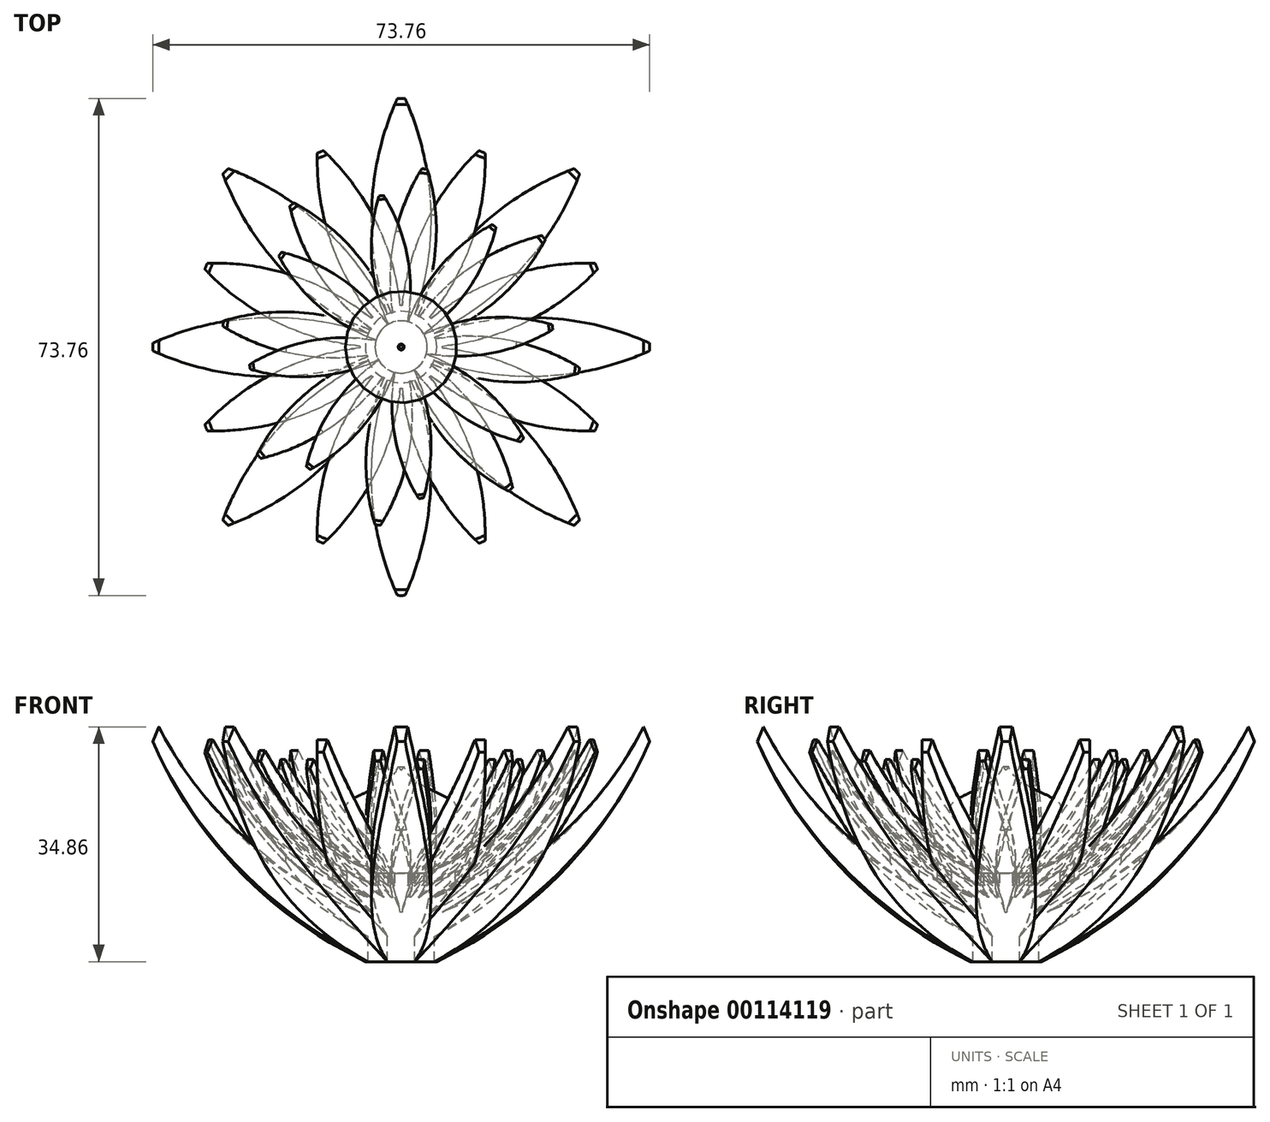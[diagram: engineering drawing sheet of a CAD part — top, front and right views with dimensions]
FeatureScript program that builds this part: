
annotation { "Feature Type Name" : "Feature", "Feature Type Description" : "" }
export const myFeature = defineFeature(function(context is Context, id is Id, definition is map)
    precondition{}
    {
        {
            var Q0;
            Q0=qCreatedBy(makeId("Top.planeOp"),FACE);
            var sketch = newSketch(context, id + "F0", { "sketchPlane" : qUnion([Q0])});
            skLineSegment(sketch, "E0.bottom", {"start": v(38.1, -38.1) * mm, "end": v(-38.1, -38.1) * mm});
            skLineSegment(sketch, "E0.top", {"start": v(38.1, 38.1) * mm, "end": v(-38.1, 38.1) * mm});
            skLineSegment(sketch, "E0.left", {"start": v(38.1, -38.1) * mm, "end": v(38.1, 38.1) * mm});
            skLineSegment(sketch, "E0.right", {"start": v(-38.1, -38.1) * mm, "end": v(-38.1, 38.1) * mm});
            skPoint(sketch, "E0.middle", {"position": v(0, 0) * mm});
            skSolve(sketch);
        }
        {
            var Q0;
            Q0 = qSketchRegion(id + "F0", true);
            extrude(context, id + "F1", {"entities" : qUnion([Q0]), "depth" : 50.8 * mm});
        }
        {
            var Q0;
            Q0=makeQuery(id+"F1.opExtrude","CAP_FACE",FACE,{"disambiguationData":[OSD([sQuery(id+"F0.wireOp",EDGE,"E0.bottom"),sQuery(id+"F0.wireOp",EDGE,"E0.top"),sQuery(id+"F0.wireOp",EDGE,"E0.left"),sQuery(id+"F0.wireOp",EDGE,"E0.right")])],"isStart":false});
            var sketch = newSketch(context, id + "F2", { "sketchPlane" : qUnion([Q0])});
            skCircle(sketch, "E1", {"center": v(0, 0) * mm, "radius": 3.18 * mm, "construction": true});
            skLineSegment(sketch, "E2", {"start": v(-38.1, 38.1) * mm, "end": v(38.1, -38.1) * mm, "construction": true});
            skLineSegment(sketch, "E3", {"start": v(38.1, 38.1) * mm, "end": v(-38.1, -38.1) * mm, "construction": true});
            skLineSegment(sketch, "E4", {"start": v(0, -38.1) * mm, "end": v(0, 38.1) * mm, "construction": true});
            skLineSegment(sketch, "E5", {"start": v(-38.1, 0) * mm, "end": v(38.1, 0) * mm, "construction": true});
            skLineSegment(sketch, "E6.bottom", {"start": v(-38.1, 38.1) * mm, "end": v(38.1, 38.1) * mm});
            skLineSegment(sketch, "E6.top", {"start": v(-38.1, -38.1) * mm, "end": v(38.1, -38.1) * mm});
            skLineSegment(sketch, "E6.left", {"start": v(-38.1, 38.1) * mm, "end": v(-38.1, -38.1) * mm});
            skLineSegment(sketch, "E6.right", {"start": v(38.1, 38.1) * mm, "end": v(38.1, -38.1) * mm});
            skArc(sketch, "E7", {"start": v(0, 0) * mm, "mid": v(4.4, 19.05) * mm, "end": v(0, 38.1) * mm});
            skArc(sketch, "E8.MirrorCS", {"start": v(0, 0) * mm, "mid": v(-4.4, 19.05) * mm, "end": v(0, 38.1) * mm});
            skArc(sketch, "E9.1.0", {"start": v(0, 0) * mm, "mid": v(-10.36, 16.58) * mm, "end": v(-26.94, 26.94) * mm});
            skArc(sketch, "E9.1.1", {"start": v(0, 0) * mm, "mid": v(-16.58, 10.36) * mm, "end": v(-26.94, 26.94) * mm});
            skArc(sketch, "E9.2.0", {"start": v(0, 0) * mm, "mid": v(-19.05, 4.4) * mm, "end": v(-38.1, 0) * mm});
            skArc(sketch, "E9.2.1", {"start": v(0, 0) * mm, "mid": v(-19.05, -4.4) * mm, "end": v(-38.1, 0) * mm});
            skArc(sketch, "E9.3.0", {"start": v(0, 0) * mm, "mid": v(-16.58, -10.36) * mm, "end": v(-26.94, -26.94) * mm});
            skArc(sketch, "E9.3.1", {"start": v(0, 0) * mm, "mid": v(-10.36, -16.58) * mm, "end": v(-26.94, -26.94) * mm});
            skArc(sketch, "E9.4.0", {"start": v(0, 0) * mm, "mid": v(-4.4, -19.05) * mm, "end": v(0, -38.1) * mm});
            skArc(sketch, "E9.4.1", {"start": v(0, 0) * mm, "mid": v(4.4, -19.05) * mm, "end": v(0, -38.1) * mm});
            skArc(sketch, "E9.5.0", {"start": v(0, 0) * mm, "mid": v(10.36, -16.58) * mm, "end": v(26.94, -26.94) * mm});
            skArc(sketch, "E9.5.1", {"start": v(0, 0) * mm, "mid": v(16.58, -10.36) * mm, "end": v(26.94, -26.94) * mm});
            skArc(sketch, "E9.6.0", {"start": v(0, 0) * mm, "mid": v(19.05, -4.4) * mm, "end": v(38.1, 0) * mm});
            skArc(sketch, "E9.6.1", {"start": v(0, 0) * mm, "mid": v(19.05, 4.4) * mm, "end": v(38.1, 0) * mm});
            skArc(sketch, "E9.7.0", {"start": v(0, 0) * mm, "mid": v(16.58, 10.36) * mm, "end": v(26.94, 26.94) * mm});
            skArc(sketch, "E9.7.1", {"start": v(0, 0) * mm, "mid": v(10.36, 16.58) * mm, "end": v(26.94, 26.94) * mm});
            skSolve(sketch);
        }
        {
            var Q0;
            {var subQ0=sQuery(id+"F2.wireOp",EDGE,"E9.1.1");var subQ1=sQuery(id+"F2.wireOp",EDGE,"E9.1.0");var subQ2=makeQuery(id+"F2.imprint","INTERSECT",VERTEX,{"derivedFrom":[subQ1,subQ0]});Q0=makeQuery(id+"F2.imprint","IMPRINT",FACE,{"disambiguationData":[TD([[makeQuery(id+"F2.imprint","IMPRINT",EDGE,{"disambiguationData":[TD([[subQ2,1.0]])],"derivedFrom":subQ1}),-1.0]])]});}
            var Q1;
            {var subQ0=sQuery(id+"F2.wireOp",EDGE,"E9.5.1");var subQ1=sQuery(id+"F2.wireOp",EDGE,"E9.5.0");var subQ2=makeQuery(id+"F2.imprint","INTERSECT",VERTEX,{"derivedFrom":[subQ1,subQ0]});Q1=makeQuery(id+"F2.imprint","IMPRINT",FACE,{"disambiguationData":[TD([[makeQuery(id+"F2.imprint","IMPRINT",EDGE,{"disambiguationData":[TD([[subQ2,1.0]])],"derivedFrom":subQ1}),-1.0]])]});}
            var Q2;
            {var subQ0=sQuery(id+"F2.wireOp",EDGE,"E9.3.1");var subQ1=sQuery(id+"F2.wireOp",EDGE,"E9.3.0");var subQ2=makeQuery(id+"F2.imprint","INTERSECT",VERTEX,{"derivedFrom":[subQ1,subQ0]});Q2=makeQuery(id+"F2.imprint","IMPRINT",FACE,{"disambiguationData":[TD([[makeQuery(id+"F2.imprint","IMPRINT",EDGE,{"disambiguationData":[TD([[subQ2,1.0]])],"derivedFrom":subQ1}),-1.0]])]});}
            var Q3;
            {var subQ3=sQuery(id+"F2.wireOp",EDGE,"E9.7.0");var subQ9=sQuery(id+"F2.wireOp",EDGE,"E9.7.1");var subQ11=makeQuery(id+"F2.imprint","INTERSECT",VERTEX,{"derivedFrom":[subQ3,subQ9]});Q3=makeQuery(id+"F2.imprint","IMPRINT",FACE,{"disambiguationData":[TD([[makeQuery(id+"F2.imprint","IMPRINT",EDGE,{"disambiguationData":[TD([[subQ11,1.0]])],"derivedFrom":subQ3}),-1.0]])]});}
            extrude(context, id + "F3", {"entities" : qUnion([Q0, Q1, Q2, Q3]), "operationType" : NewBodyOperationType.REMOVE, "endBound" : BoundingType.THROUGH_ALL, "oppositeDirection" : true, "depth" : 25.4 * mm});
        }
        {
            var Q0;
            Q0=qCreatedBy(makeId("Front.planeOp"),FACE);
            var sketch = newSketch(context, id + "F4", { "sketchPlane" : qUnion([Q0])});
            skLineSegment(sketch, "E10", {"start": v(0, 0) * mm, "end": v(0, 58.2) * mm, "construction": true});
            skPoint(sketch, "E11.0", {"position": v(-38.1, 50.8) * mm});
            skPoint(sketch, "E11.1", {"position": v(38.1, 50.8) * mm});
            skPoint(sketch, "E11.2", {"position": v(38.1, 0) * mm});
            skPoint(sketch, "E11.3", {"position": v(-38.1, 0) * mm});
            skLineSegment(sketch, "E12.bottom", {"start": v(-38.1, 50.8) * mm, "end": v(38.1, 50.8) * mm, "construction": true});
            skLineSegment(sketch, "E12.top", {"start": v(-38.1, 0) * mm, "end": v(38.1, 0) * mm, "construction": true});
            skLineSegment(sketch, "E12.left", {"start": v(-38.1, 50.8) * mm, "end": v(-38.1, 0) * mm, "construction": true});
            skLineSegment(sketch, "E12.right", {"start": v(38.1, 50.8) * mm, "end": v(38.1, 0) * mm, "construction": true});
            skArc(sketch, "E13", {"start": v(-36, 37.1) * mm, "mid": v(-21.13, 18.5) * mm, "end": v(0, 7.51) * mm});
            skArc(sketch, "E14", {"start": v(-36.88, 34.9) * mm, "mid": v(-21.98, 13.7) * mm, "end": v(0, 0) * mm});
            skLineSegment(sketch, "E15.bottom", {"start": v(0, 64) * mm, "end": v(-47.12, 64) * mm});
            skLineSegment(sketch, "E15.top", {"start": v(0, -8.54) * mm, "end": v(-47.12, -8.54) * mm});
            skLineSegment(sketch, "E15.left", {"start": v(0, 64) * mm, "end": v(0, -8.54) * mm});
            skLineSegment(sketch, "E15.right", {"start": v(-47.12, 64) * mm, "end": v(-47.12, -8.54) * mm});
            skLineSegment(sketch, "E16", {"start": v(-36, 37.1) * mm, "end": v(-36.88, 34.9) * mm});
            skLineSegment(sketch, "E17", {"start": v(0, 7.51) * mm, "end": v(0, 0) * mm});
            skSolve(sketch);
        }
        {
            var Q0;
            {var subQ4=sQuery(id+"F4.wireOp",EDGE,"E13");Q0=makeQuery(id+"F4.imprint","IMPRINT",FACE,{"disambiguationData":[TD([[makeQuery(id+"F4.imprint","IMPRINT",EDGE,{"derivedFrom":subQ4}),1.0]])]});}
            var Q1;
            Q1=sQuery(id+"F4.wireOp",EDGE,"E15.left");
            revolve(context, id + "F5", {"operationType" : NewBodyOperationType.REMOVE, "entities" : qUnion([Q0]), "axis" : qUnion([Q1]), "revolveType" : RevolveType.FULL, "oppositeDirection" : true});
        }
        {
            var Q0;
            Q0=qCreatedBy(makeId("Front.planeOp"),FACE);
            var sketch = newSketch(context, id + "F6", { "sketchPlane" : qUnion([Q0])});
            skLineSegment(sketch, "E18", {"start": v(0, 0) * mm, "end": v(0, 66.84) * mm, "construction": true});
            skSolve(sketch);
        }
        {
            var Q0;
            Q0=makeQuery(id+"F1.opExtrude","SWEPT_BODY",BODY,{"disambiguationData":[OSD([sQuery(id+"F0.wireOp",EDGE,"E0.bottom"),sQuery(id+"F0.wireOp",EDGE,"E0.top"),sQuery(id+"F0.wireOp",EDGE,"E0.left"),sQuery(id+"F0.wireOp",EDGE,"E0.right")])]});
            transform(context, id + "F7", {"entities" : qUnion([Q0]), "transformType" : TransformType.TRANSLATION_3D, "dx" : 0 * mm, "dy" : 0 * mm, "dz" : 4.32 * mm, "makeCopy" : true});
        }
        {
            var Q0;
            Q0=makeQuery(id+"F7.opPattern","COPY",BODY,{"derivedFrom":makeQuery(id+"F1.opExtrude","SWEPT_BODY",BODY,{"disambiguationData":[OSD([sQuery(id+"F0.wireOp",EDGE,"E0.bottom"),sQuery(id+"F0.wireOp",EDGE,"E0.top"),sQuery(id+"F0.wireOp",EDGE,"E0.left"),sQuery(id+"F0.wireOp",EDGE,"E0.right")])]}),"instanceName":"1"});
            var Q1;
            Q1=sQuery(id+"F6.wireOp",EDGE,"E18");
            transform(context, id + "F8", {"entities" : qUnion([Q0]), "transformType" : TransformType.ROTATION, "transformAxis" : qUnion([Q1]), "angle" : 22.5 * degree, "makeCopy" : false});
        }
        {
            var Q0;
            Q0=makeQuery(id+"F7.opPattern","COPY",BODY,{"derivedFrom":makeQuery(id+"F1.opExtrude","SWEPT_BODY",BODY,{"disambiguationData":[OSD([sQuery(id+"F0.wireOp",EDGE,"E0.bottom"),sQuery(id+"F0.wireOp",EDGE,"E0.top"),sQuery(id+"F0.wireOp",EDGE,"E0.left"),sQuery(id+"F0.wireOp",EDGE,"E0.right")])]}),"instanceName":"1"});
            var Q1;
            Q1=qCreatedBy(makeId("Origin.pointOp"),VERTEX);
            transform(context, id + "F9", {"entities" : qUnion([Q0]), "transformType" : TransformType.SCALE_UNIFORMLY, "scale" : .85, "scalePoint" : qUnion([Q1]), "makeCopy" : false});
        }
        {
            var Q0;
            Q0=makeQuery(id+"F7.opPattern","COPY",BODY,{"derivedFrom":makeQuery(id+"F1.opExtrude","SWEPT_BODY",BODY,{"disambiguationData":[OSD([sQuery(id+"F0.wireOp",EDGE,"E0.bottom"),sQuery(id+"F0.wireOp",EDGE,"E0.top"),sQuery(id+"F0.wireOp",EDGE,"E0.left"),sQuery(id+"F0.wireOp",EDGE,"E0.right")])]}),"instanceName":"1"});
            transform(context, id + "F10", {"entities" : qUnion([Q0]), "transformType" : TransformType.TRANSLATION_3D, "dx" : 0 * mm, "dy" : 0 * mm, "dz" : 4.32 * mm, "makeCopy" : true});
        }
        {
            var Q0;
            Q0=makeQuery(id+"F10.opPattern","COPY",BODY,{"derivedFrom":makeQuery(id+"F7.opPattern","COPY",BODY,{"derivedFrom":makeQuery(id+"F1.opExtrude","SWEPT_BODY",BODY,{"disambiguationData":[OSD([sQuery(id+"F0.wireOp",EDGE,"E0.bottom"),sQuery(id+"F0.wireOp",EDGE,"E0.top"),sQuery(id+"F0.wireOp",EDGE,"E0.left"),sQuery(id+"F0.wireOp",EDGE,"E0.right")])]}),"instanceName":"1"}),"instanceName":"1"});
            var Q1;
            Q1=sQuery(id+"F6.wireOp",EDGE,"E18");
            transform(context, id + "F11", {"entities" : qUnion([Q0]), "transformType" : TransformType.ROTATION, "transformAxis" : qUnion([Q1]), "angle" : 60 * degree, "makeCopy" : false});
        }
        {
            var Q0;
            Q0=makeQuery(id+"F10.opPattern","COPY",BODY,{"derivedFrom":makeQuery(id+"F7.opPattern","COPY",BODY,{"derivedFrom":makeQuery(id+"F1.opExtrude","SWEPT_BODY",BODY,{"disambiguationData":[OSD([sQuery(id+"F0.wireOp",EDGE,"E0.bottom"),sQuery(id+"F0.wireOp",EDGE,"E0.top"),sQuery(id+"F0.wireOp",EDGE,"E0.left"),sQuery(id+"F0.wireOp",EDGE,"E0.right")])]}),"instanceName":"1"}),"instanceName":"1"});
            var Q1;
            Q1=sQuery(id+"F6.wireOp",VERTEX,"E18.start");
            transform(context, id + "F12", {"entities" : qUnion([Q0]), "transformType" : TransformType.SCALE_UNIFORMLY, "scale" : .85, "scalePoint" : qUnion([Q1]), "makeCopy" : false});
        }
        {
            var Q0;
            Q0=makeQuery(id+"F10.opPattern","COPY",BODY,{"derivedFrom":makeQuery(id+"F7.opPattern","COPY",BODY,{"derivedFrom":makeQuery(id+"F1.opExtrude","SWEPT_BODY",BODY,{"disambiguationData":[OSD([sQuery(id+"F0.wireOp",EDGE,"E0.bottom"),sQuery(id+"F0.wireOp",EDGE,"E0.top"),sQuery(id+"F0.wireOp",EDGE,"E0.left"),sQuery(id+"F0.wireOp",EDGE,"E0.right")])]}),"instanceName":"1"}),"instanceName":"1"});
            transform(context, id + "F13", {"entities" : qUnion([Q0]), "transformType" : TransformType.TRANSLATION_3D, "dx" : 0 * mm, "dy" : 0 * mm, "dz" : 4.32 * mm, "makeCopy" : true});
        }
        {
            var Q0;
            Q0=makeQuery(id+"F13.opPattern","COPY",BODY,{"derivedFrom":makeQuery(id+"F10.opPattern","COPY",BODY,{"derivedFrom":makeQuery(id+"F7.opPattern","COPY",BODY,{"derivedFrom":makeQuery(id+"F1.opExtrude","SWEPT_BODY",BODY,{"disambiguationData":[OSD([sQuery(id+"F0.wireOp",EDGE,"E0.bottom"),sQuery(id+"F0.wireOp",EDGE,"E0.top"),sQuery(id+"F0.wireOp",EDGE,"E0.left"),sQuery(id+"F0.wireOp",EDGE,"E0.right")])]}),"instanceName":"1"}),"instanceName":"1"}),"instanceName":"1"});
            var Q1;
            Q1=sQuery(id+"F6.wireOp",EDGE,"E18");
            transform(context, id + "F14", {"entities" : qUnion([Q0]), "transformType" : TransformType.ROTATION, "transformAxis" : qUnion([Q1]), "angle" : 60 * degree, "makeCopy" : false});
        }
        {
            var Q0;
            Q0=makeQuery(id+"F13.opPattern","COPY",BODY,{"derivedFrom":makeQuery(id+"F10.opPattern","COPY",BODY,{"derivedFrom":makeQuery(id+"F7.opPattern","COPY",BODY,{"derivedFrom":makeQuery(id+"F1.opExtrude","SWEPT_BODY",BODY,{"disambiguationData":[OSD([sQuery(id+"F0.wireOp",EDGE,"E0.bottom"),sQuery(id+"F0.wireOp",EDGE,"E0.top"),sQuery(id+"F0.wireOp",EDGE,"E0.left"),sQuery(id+"F0.wireOp",EDGE,"E0.right")])]}),"instanceName":"1"}),"instanceName":"1"}),"instanceName":"1"});
            var Q1;
            Q1=sQuery(id+"F6.wireOp",VERTEX,"E18.start");
            transform(context, id + "F15", {"entities" : qUnion([Q0]), "transformType" : TransformType.SCALE_UNIFORMLY, "scale" : .85, "scalePoint" : qUnion([Q1]), "makeCopy" : false});
        }
        {
            var Q0;
            Q0=qCreatedBy(makeId("Front.planeOp"),FACE);
            var sketch = newSketch(context, id + "F16", { "sketchPlane" : qUnion([Q0])});
            skLineSegment(sketch, "E19", {"start": v(-0.45, 31.16) * mm, "end": v(-0.45, 15.6) * mm, "construction": true});
            skFitSpline(sketch, "E20", {"points": [v(0, 15.09) * mm, v(-8.18, 25.4) * mm, v(-0.45, 31.16) * mm], "startDerivative": vector(-17.53, 26.01) * mm, "endDerivative": vector(7.37, 21.07) * mm});
            skLineSegment(sketch, "E21", {"start": v(0, 15.09) * mm, "end": v(0, 31.16) * mm});
            skLineSegment(sketch, "E22", {"start": v(-0.45, 31.16) * mm, "end": v(-0.3, 31.16) * mm});
            skArc(sketch, "E23", {"start": v(-0.3, 31.16) * mm, "mid": v(-0.22, 30.89) * mm, "end": v(0, 30.71) * mm});
            skLineSegment(sketch, "E24", {"start": v(-3.87, 20.53) * mm, "end": v(-3.87, 3.85) * mm});
            skLineSegment(sketch, "E25", {"start": v(-3.87, 3.85) * mm, "end": v(0, 3.85) * mm});
            skLineSegment(sketch, "E26", {"start": v(0, 3.85) * mm, "end": v(0, 18.29) * mm});
            skSolve(sketch);
        }
        {
            var Q0;
            Q0 = qSketchRegion(id + "F16", true);
            var Q1;
            Q1=sQuery(id+"F16.wireOp",EDGE,"E21");
            revolve(context, id + "F17", {"operationType" : NewBodyOperationType.ADD, "entities" : qUnion([Q0]), "axis" : qUnion([Q1]), "revolveType" : RevolveType.FULL});
        }
        {
            var Q0;
            Q0=qCreatedBy(makeId("Top.planeOp"),FACE);
            var sketch = newSketch(context, id + "F18", { "sketchPlane" : qUnion([Q0])});
            skCircle(sketch, "E27", {"center": v(0, 0) * mm, "radius": 6.35 * mm});
            skSolve(sketch);
        }
        {
            var Q0;
            Q0=makeQuery(id+"F17.opRevolve","SWEPT_EDGE",EDGE,{"disambiguationData":[OSD([sQuery(id+"F16.wireOp",EDGE,"E20"),sQuery(id+"F16.wireOp",EDGE,"E24")])]});
            fillet(context, id + "F19", {"entities" : qUnion([Q0]), "radius" : 5.08 * mm, "tangentPropagation" : true, "allowEdgeOverflow" : false});
        }
        {
            var Q0;
            Q0 = qSketchRegion(id + "F18", true);
            extrude(context, id + "F20", {"entities" : qUnion([Q0]), "operationType" : NewBodyOperationType.REMOVE, "depth" : 2.25 * mm});
        }
    });
